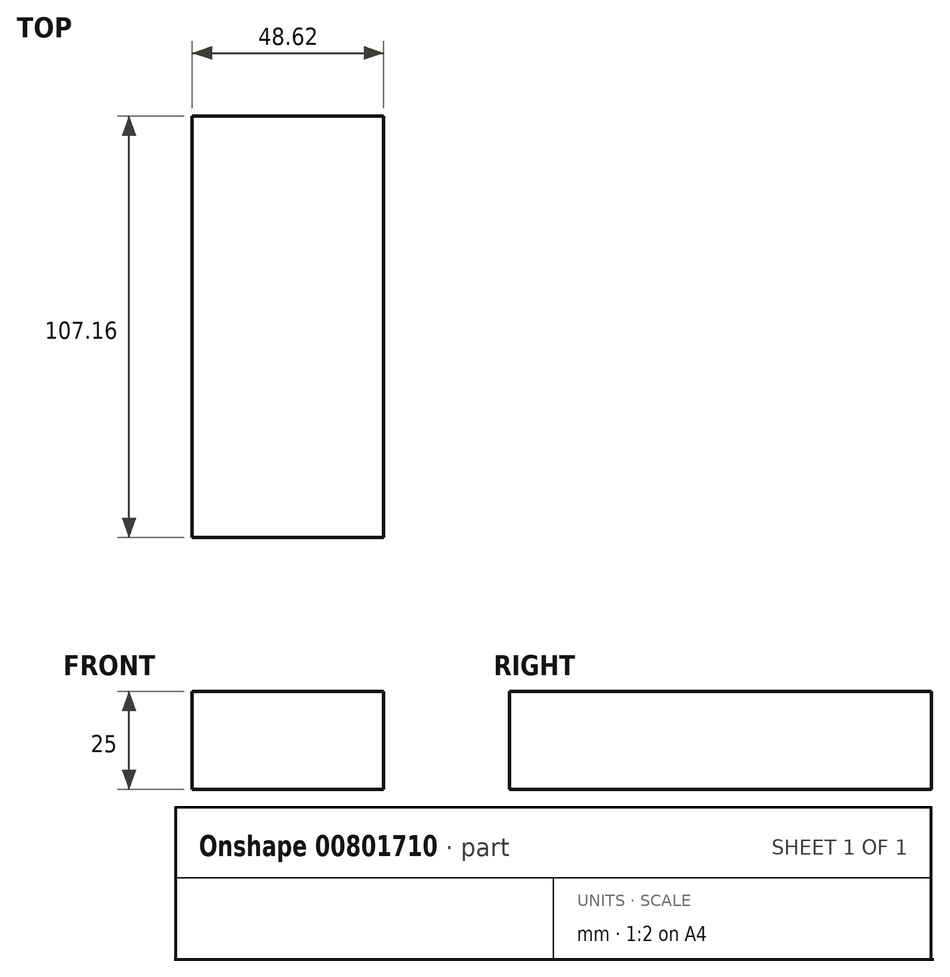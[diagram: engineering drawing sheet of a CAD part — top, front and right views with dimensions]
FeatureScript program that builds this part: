
annotation { "Feature Type Name" : "Feature", "Feature Type Description" : "" }
export const myFeature = defineFeature(function(context is Context, id is Id, definition is map)
    precondition{}
    {
        {
            var Q0;
            Q0=qCreatedBy(makeId("Top.planeOp"),FACE);
            var sketch = newSketch(context, id + "F0", { "sketchPlane" : qUnion([Q0])});
            skLineSegment(sketch, "E0.bottom", {"start": v(0, 0) * mm, "end": v(48.62, 0) * mm});
            skLineSegment(sketch, "E0.top", {"start": v(0, 107.16) * mm, "end": v(48.62, 107.16) * mm});
            skLineSegment(sketch, "E0.left", {"start": v(0, 0) * mm, "end": v(0, 107.16) * mm});
            skLineSegment(sketch, "E0.right", {"start": v(48.62, 0) * mm, "end": v(48.62, 107.16) * mm});
            skSolve(sketch);
        }
        {
            var Q0;
            Q0=makeQuery(id+"F0.imprint","IMPRINT",FACE,{"disambiguationData":[TD([[makeQuery(id+"F0.imprint","IMPRINT",EDGE,{"derivedFrom":sQuery(id+"F0.wireOp",EDGE,"E0.bottom")}),1.0]])]});
            extrude(context, id + "F1", {"entities" : qUnion([Q0]), "depth" : 25 * mm, "offsetDistance" : 25 * mm});
        }
    });
